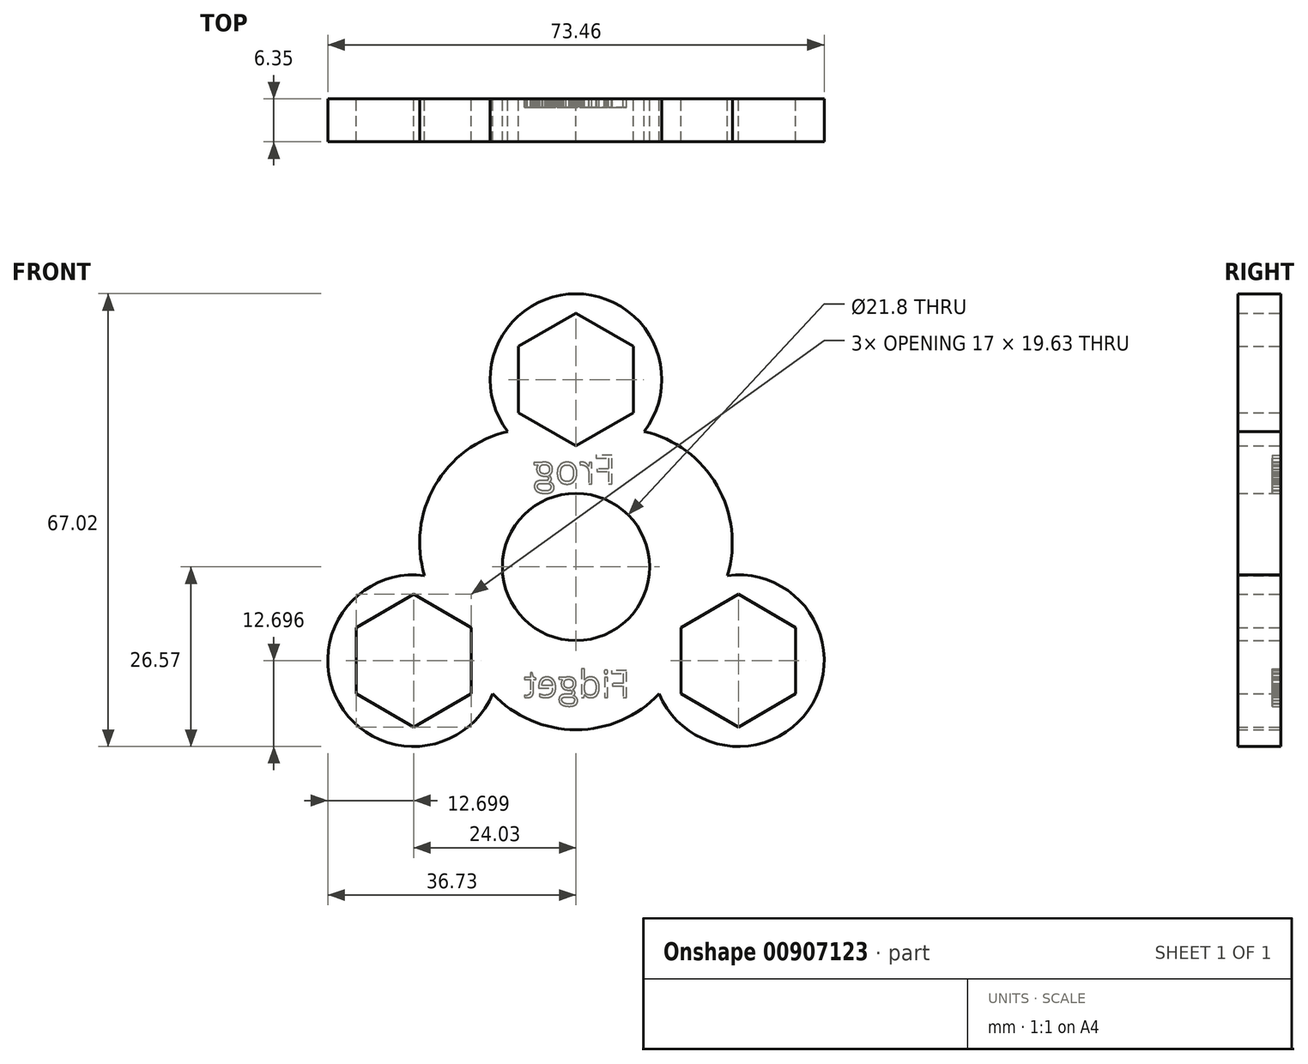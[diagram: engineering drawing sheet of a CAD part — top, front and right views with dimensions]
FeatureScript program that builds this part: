
annotation { "Feature Type Name" : "Feature", "Feature Type Description" : "" }
export const myFeature = defineFeature(function(context is Context, id is Id, definition is map)
    precondition{}
    {
        {
            var Q0;
            Q0=qCreatedBy(makeId("Front.planeOp"),FACE);
            var sketch = newSketch(context, id + "F0", { "sketchPlane" : qUnion([Q0])});
            skCircle(sketch, "E0", {"center": v(0, 0) * mm, "radius": 10.9 * mm});
            skCircle(sketch, "E1", {"center": v(0, 27.75) * mm, "radius": 12.7 * mm});
            skCircle(sketch, "E2.1.0", {"center": v(-24.03, -13.87) * mm, "radius": 12.7 * mm});
            skCircle(sketch, "E2.2.0", {"center": v(24.03, -13.87) * mm, "radius": 12.7 * mm});
            skCircle(sketch, "E3.cCircle", {"center": v(-24.03, -13.87) * mm, "radius": 8.5 * mm, "construction": true});
            skLineSegment(sketch, "E3.0", {"start": v(-15.53, -8.97) * mm, "end": v(-15.53, -18.78) * mm});
            skLineSegment(sketch, "E3.1", {"start": v(-15.53, -18.78) * mm, "end": v(-24.03, -23.69) * mm});
            skLineSegment(sketch, "E3.2", {"start": v(-24.03, -23.69) * mm, "end": v(-32.53, -18.78) * mm});
            skLineSegment(sketch, "E3.3", {"start": v(-32.53, -18.78) * mm, "end": v(-32.53, -8.97) * mm});
            skLineSegment(sketch, "E3.4", {"start": v(-32.53, -8.97) * mm, "end": v(-24.03, -4.06) * mm});
            skLineSegment(sketch, "E3.5", {"start": v(-24.03, -4.06) * mm, "end": v(-15.53, -8.97) * mm});
            skPoint(sketch, "E3.0.midPoint", {"position": v(-15.53, -13.87) * mm});
            skCircle(sketch, "E4.1.0", {"center": v(24.03, -13.87) * mm, "radius": 8.5 * mm, "construction": true});
            skLineSegment(sketch, "E4.1.1", {"start": v(24.03, -4.06) * mm, "end": v(32.53, -8.97) * mm});
            skLineSegment(sketch, "E4.1.2", {"start": v(15.53, -8.97) * mm, "end": v(24.03, -4.06) * mm});
            skLineSegment(sketch, "E4.1.3", {"start": v(15.53, -18.78) * mm, "end": v(15.53, -8.97) * mm});
            skLineSegment(sketch, "E4.1.4", {"start": v(24.03, -23.69) * mm, "end": v(15.53, -18.78) * mm});
            skLineSegment(sketch, "E4.1.5", {"start": v(32.53, -18.78) * mm, "end": v(24.03, -23.69) * mm});
            skLineSegment(sketch, "E4.1.6", {"start": v(32.53, -8.97) * mm, "end": v(32.53, -18.78) * mm});
            skCircle(sketch, "E4.2.0", {"center": v(0, 27.75) * mm, "radius": 8.5 * mm, "construction": true});
            skLineSegment(sketch, "E4.2.1", {"start": v(-8.5, 22.84) * mm, "end": v(-8.5, 32.66) * mm});
            skLineSegment(sketch, "E4.2.2", {"start": v(0, 17.93) * mm, "end": v(-8.5, 22.84) * mm});
            skLineSegment(sketch, "E4.2.3", {"start": v(8.5, 22.84) * mm, "end": v(0, 17.93) * mm});
            skLineSegment(sketch, "E4.2.4", {"start": v(8.5, 32.66) * mm, "end": v(8.5, 22.84) * mm});
            skLineSegment(sketch, "E4.2.5", {"start": v(0, 37.56) * mm, "end": v(8.5, 32.66) * mm});
            skLineSegment(sketch, "E4.2.6", {"start": v(-8.5, 32.66) * mm, "end": v(0, 37.56) * mm});
            skArc(sketch, "E5", {"start": v(-12.32, -18.78) * mm, "mid": v(0, -24.1) * mm, "end": v(12.32, -18.78) * mm});
            skArc(sketch, "E6.1.0", {"start": v(22.42, -1.28) * mm, "mid": v(20.87, 12.05) * mm, "end": v(10.1, 20.06) * mm});
            skArc(sketch, "E6.2.0", {"start": v(-10.1, 20.06) * mm, "mid": v(-20.87, 12.05) * mm, "end": v(-22.42, -1.28) * mm});
            skSolve(sketch);
        }
        {
            var Q0;
            Q0 = qSketchRegion(id + "F0", true);
            extrude(context, id + "F1", {"entities" : qUnion([Q0]), "depth" : 6.35 * mm, "offsetDistance" : 25.4 * mm});
        }
        {
            var Q0;
            Q0=makeQuery(id+"F1.opExtrude","CAP_FACE",FACE,{"disambiguationData":[OSD([sQuery(id+"F0.wireOp",EDGE,"E0"),sQuery(id+"F0.wireOp",EDGE,"E1"),sQuery(id+"F0.wireOp",EDGE,"E2.1.0"),sQuery(id+"F0.wireOp",EDGE,"E2.2.0"),sQuery(id+"F0.wireOp",EDGE,"E3.0"),sQuery(id+"F0.wireOp",EDGE,"E3.1"),sQuery(id+"F0.wireOp",EDGE,"E3.2"),sQuery(id+"F0.wireOp",EDGE,"E3.3"),sQuery(id+"F0.wireOp",EDGE,"E3.4"),sQuery(id+"F0.wireOp",EDGE,"E3.5"),sQuery(id+"F0.wireOp",EDGE,"E4.1.1"),sQuery(id+"F0.wireOp",EDGE,"E4.1.2"),sQuery(id+"F0.wireOp",EDGE,"E4.1.3"),sQuery(id+"F0.wireOp",EDGE,"E4.1.4"),sQuery(id+"F0.wireOp",EDGE,"E4.1.5"),sQuery(id+"F0.wireOp",EDGE,"E4.1.6"),sQuery(id+"F0.wireOp",EDGE,"E4.2.1"),sQuery(id+"F0.wireOp",EDGE,"E4.2.2"),sQuery(id+"F0.wireOp",EDGE,"E4.2.3"),sQuery(id+"F0.wireOp",EDGE,"E4.2.4"),sQuery(id+"F0.wireOp",EDGE,"E4.2.5"),sQuery(id+"F0.wireOp",EDGE,"E4.2.6"),sQuery(id+"F0.wireOp",EDGE,"E5"),sQuery(id+"F0.wireOp",EDGE,"E6.1.0"),sQuery(id+"F0.wireOp",EDGE,"E6.2.0")])],"isStart":true});
            var sketch = newSketch(context, id + "F2", { "sketchPlane" : qUnion([Q0])});
            skText(sketch, "E7", { "text": "Fidget", "fontName": "OpenSans-Regular.ttf"});
            skText(sketch, "E8", { "text": "Frog", "fontName": "OpenSans-Regular.ttf"});
            const initialGuessF2  = {"E7": [-0.008, -0.01931, 1, 0, 0.00399], "E8": [-0.00591, 0.0123, 1, 0, 0.00425]};
            skSetInitialGuess(sketch, initialGuessF2);
            skSolve(sketch);
        }
        {
            var Q0;
            Q0 = qSketchRegion(id + "F2", true);
            extrude(context, id + "F3", {"entities" : qUnion([Q0]), "operationType" : NewBodyOperationType.REMOVE, "oppositeDirection" : true, "depth" : 1.27 * mm, "offsetDistance" : 25.4 * mm});
        }
    });
